# Revit family: Mate_side_table_SC73
name_source: partatom
category: Furniture
revit_build: Autodesk Revit 2017 (Build: 20171027_0315(x64)
units: mm (PartAtom-declared; Revit-internal decimal feet)

## family parameters
Always vertical = Yes
Cut with Voids When Loaded = No
OmniClass Number = 23.40.20.00
OmniClass Title = General Furniture and Specialties
Room Calculation Point = No
Shared = No
Work Plane-Based = No

## types (1)
- Mate_side_table_SC73
    Base = &tradition Powder Coated Steel White 9001 Semi Matt Finish
    Depth = 35cm / 13.7in
    Description = The Mate’s unassuming appearance belies its highly functional design. Inspired by the Japanese art of origami, the table was crafted from a single sheet of powder-coated steel that was welded into shape. Designed to suit a wide variety of purposes – from an office trolley, to a bedside table or bathroom storage unit – this asymmetrical, open-faced piece can be inserted into any space. It is available in three warm, earthy tones – Black, Terracotta, and Hunter – and its dimensions are H: 60 x 35.4 x 35.4cm.
    Design = Space Copenhagen
    Design Year = 2022
    Height = 59cm / 23.2in
    Manufacturer = &tradition
    Model = Mate SC73
    Packaging Dimensions = H: 52cm/20.5in, W: 42cm/16.5in, D: 42cm/16.5in
    Type Comments = Space Copenhagen Series
    URL = https://www.andtradition.com
    Variations Colour = Please visit our website to see available colours and finishes.
    Weight = 14,8 kg
    Wheel = &tradition Plastic White 9001 Matt
    Width = 35cm / 13.7in

## geometry (parser evidence)
native form markers: Sweep x2
no freeform markers — native parametric forms only
